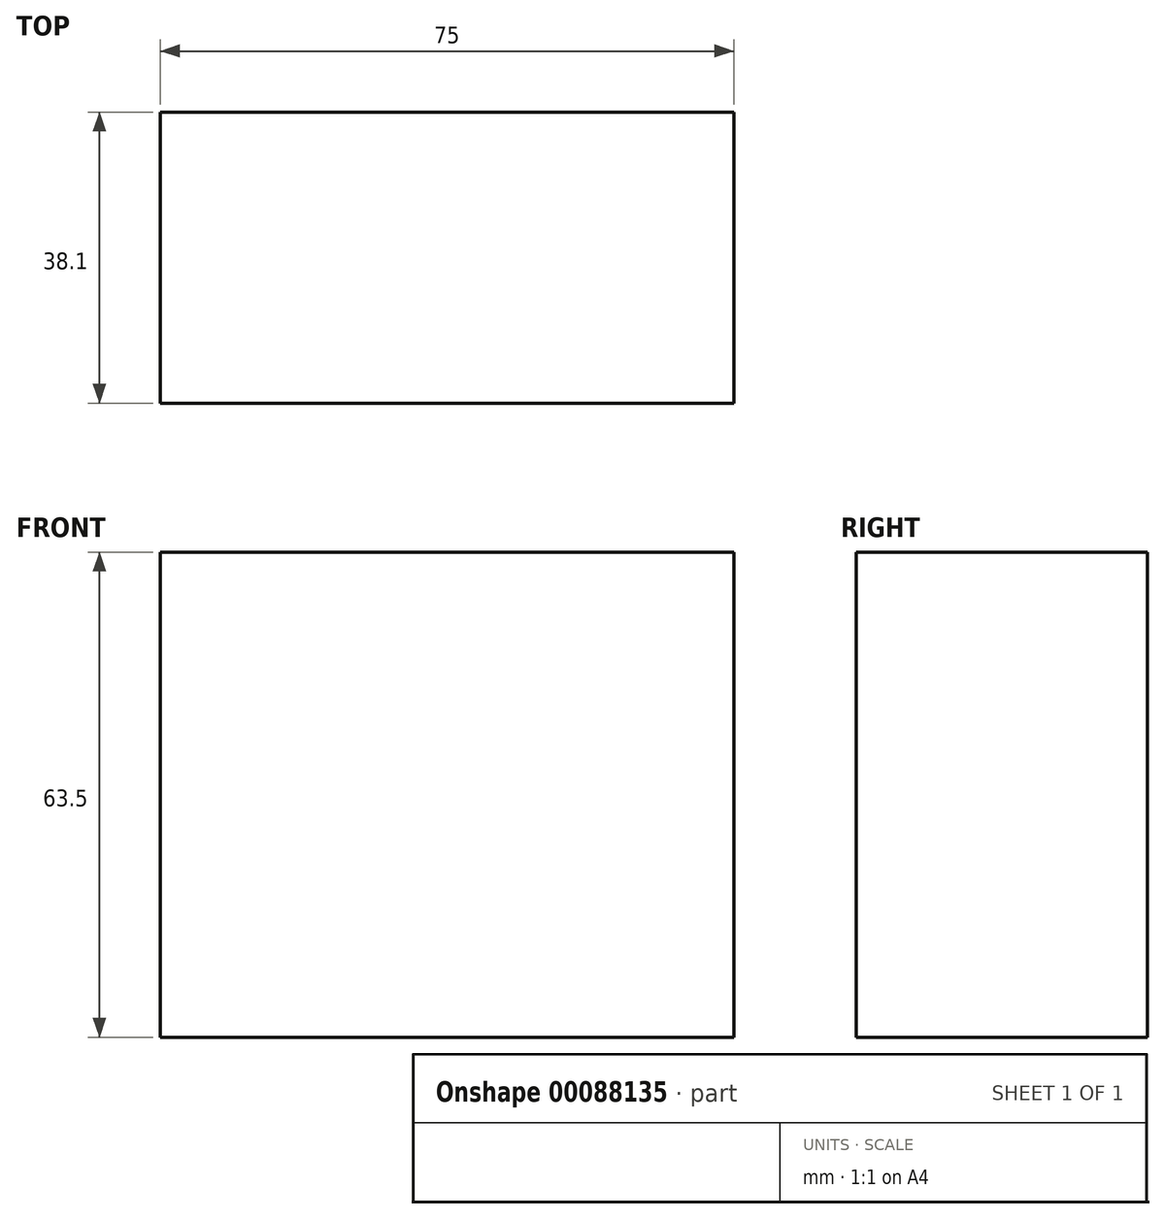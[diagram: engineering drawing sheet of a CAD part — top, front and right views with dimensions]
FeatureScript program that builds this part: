
annotation { "Feature Type Name" : "Feature", "Feature Type Description" : "" }
export const myFeature = defineFeature(function(context is Context, id is Id, definition is map)
    precondition{}
    {
        {
            var Q0;
            Q0=qCreatedBy(makeId("Top.planeOp"),FACE);
            var sketch = newSketch(context, id + "F0", { "sketchPlane" : qUnion([Q0])});
            skLineSegment(sketch, "E0.bottom", {"start": v(0, 0) * mm, "end": v(75, 0) * mm});
            skLineSegment(sketch, "E0.top", {"start": v(0, -38.1) * mm, "end": v(75, -38.1) * mm});
            skLineSegment(sketch, "E0.left", {"start": v(0, 0) * mm, "end": v(0, -38.1) * mm});
            skLineSegment(sketch, "E0.right", {"start": v(75, 0) * mm, "end": v(75, -38.1) * mm});
            skSolve(sketch);
        }
        {
            var Q0;
            Q0 = qSketchRegion(id + "F0", true);
            extrude(context, id + "F1", {"entities" : qUnion([Q0]), "depth" : 63.5 * mm});
        }
    });
